# Revit family: PG-3000_vereinfacht
name_source: partatom
category: Allgemeines Modell
revit_build: Autodesk Revit 2018 (Build: 20170223_1515(x64)
units: mm (PartAtom-declared; Revit-internal decimal feet)

## family parameters
Beim Laden mit Abzugskörper schneiden = Ja
Bemaßung runder Anschluss = Durchmesser verwenden
Gemeinsam genutzt = Ja
Kann Basisbauteil für Bewehrung sein = Nein
OmniClass-Nummer = 23.70.50.00
OmniClass-Titel = Liquid Waste Handling Services
Raumberechnungspunkt = Nein
Teiletyp = Normal

## types (1)
- MEADrain PG 3000 vereinfacht
    Artikelnummer = 010155694
    Ausführungsunterlagen = gemäß Zeichnung und Einzelbeschreibung
    Bauelement = Entwässerungsrinnen Oberflächenwasser
    Baustoff,Bettung/Fundament = PCC-Mörtel/Epoxy-Mörtel
    Bauteil, Entwässerung = Entwässerungsrinne
    Belastungsklasse Entwässerungsbauteil = C 250
    Beschreibung = Monolithische Entwässerungsrinnen aus Polymerbeton Bauhöhe 50 mm
    Breite = 300 mm
    Einbautechnologie = Rinne allein
    Gewicht = 22.8KGM
    Hersteller = MEA Bautechnik GmbH Geschäftsbereich MEA Water Management
    Höhe = 50 mm  [stored 0.164042 ft]
    IfcDescription = Monolithische Entwässerungsrinnen aus Polymerbeton Bauhöhe 50 mm
    IfcExportAs = IfcWasteTerminalType
    IfcExportType = USERDEFINED
    Konstruktion Entwässerungsbauteil = Kammrinne
    MEA Planungshilfe = https://www.mea-group.com
    Material = Polymerbeton
    Nennweite = 300 mm
    Nennweite mm Entwässerungsbauteil = 300
    STLB-Bau Mustervorlage = https://www.stlb-bau-online.de
    Technische Produktinformation = https://www.mea-group.com
    Typ Entwässerungsbauteil = Typ M
    URL = https://www.mea-group.com
    guid = cf6c1bd8-9bf4-4563-8c57-07955e2378ac

note: [stored X ft] marks values corroborated as IEEE doubles in the binary element streams (Revit-internal decimal feet)

## geometry (parser evidence)
native form markers: Extrusion x4
no freeform markers — native parametric forms only
